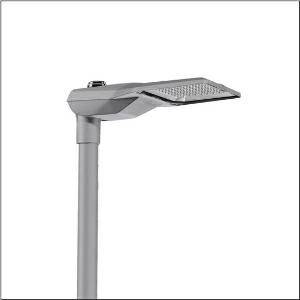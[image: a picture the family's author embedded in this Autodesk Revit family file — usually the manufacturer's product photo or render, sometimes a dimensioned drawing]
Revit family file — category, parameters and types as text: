
# Revit family: streetlight_sl_21_midi___pl52_5xe7h47n08mb_5c45
name_source: partatom
category: Lighting Fixtures
units: mm (PartAtom-declared; Revit-internal decimal feet)

## family parameters
Cut with Voids When Loaded = No
Host = Face
Light Source = No
Part Type = Normal
Room Calculation Point = No
Round Connector Dimension = Use Diameter
Shared = No

## types (1)
- --- (1 x LED, 19830 lm, 147 W, 4000K)
    Apparent Load = 147 VA
    CIE Flux Codes = 27 59 98 100 100
    Color Rendering = 70
    Color Temperature = 4000K
    Default Elevation = 1800 mm
    Description = Streetlight SL 21 midi, mast luminaire, primary light control with lens, of PMMA, primary optical cover: cover, of toughened safety glass, transparent, light distribution: PL52, light emission: direct distribution, primary light characteristic: asymmetric, installation type: side-entry, LED, 3G 2.5mm², High Power LED, rated luminous flux: 19.830lm, luminous efficacy: 135lm/W, light colour: 740, colour temperature: 4000K, control gear: NEMA (7pin), control: overheat protection, pre-setting: linear dimming characteristic, constant luminous flux control, time-dependent luminous flux control, flexible luminous flux parameterisation, mains connection: 220..240V, AC, 50/60Hz, connection cable pre-assembled, cable length: 12,5m, wiring characteristics: H05VV-F, start of lifetime: 147W, end of service life: 155W, reduction: 65W, luminaire housing, of diecast aluminium (EN AC-44300), powder-coated, Siteco® metallic grey (DB 702S), corrosivity category C5 mid according to DIN EN ISO 12944, multi-level sealing system, sealing non-destructively replaceable, inclination adjustable: 0°, 5°, 10°, 15°, length: 644mm, width: 335mm, height: 110mm, spigot size: 42mm (side-entry), mounting height: 4..8m, protection rating (complete): IP66, insulation class (complete): insulation class I (protective earthing), certification: CE, ENEC, ENEC+, VDE, impact resistance: IK09, permissible operating ambient temperature for outdoor applications: -40..+50°C, standard-compliant lighting for roads and squares, packaging unit: 1 piece

Light Distribution: PL52
    Height = 111 mm
    Lamp = 1 x LED
    Lamp Light Flux = 19830 lm
    Lamp Power = 147 W
    Lamp count = 1
    Length = 644 mm
    Luminous efficacy = 135 lm/W
    Manufacturer = Siteco
    ModVariant = No
    Model = 5XE7H47N08MB
    Number of Poles = 1
    OnlyDefault = Yes
    Power Factor = 1
    Product Name = Streetlight SL 21 midi | PL52
    Product group = mast luminaire | pylon top
    ProductGroupID = 6100
    Protection Class = Protection class I
    Protection Degree = IP 66
    RLX_Detail_Level = 1
    RLX_Emergency_Light_Flux = 0 lm
    RLX_Emergency_Type = 0
    RLX_Emergency_Type_DB = No
    RlxData = <blob elided: 99709 chars, md5=6bed973b>
    Socket = socket
    Standby Power = 0 W
    System Light Flux = 19830 lm
    System Power = 147 W
    Type Comments = factory setting: luminous flux: 100 % | dim-lin: 254 | 750 mA
    Type Image = l_1294377.jpg
    URL = http://relux.com
    VarID = @adj_132116
    Voltage = 0 V
    Weight = 0.00 kg
    Width = 336 mm

## geometry (parser evidence)
native form markers: Blend x4, Sweep x12
no freeform markers — native parametric forms only
